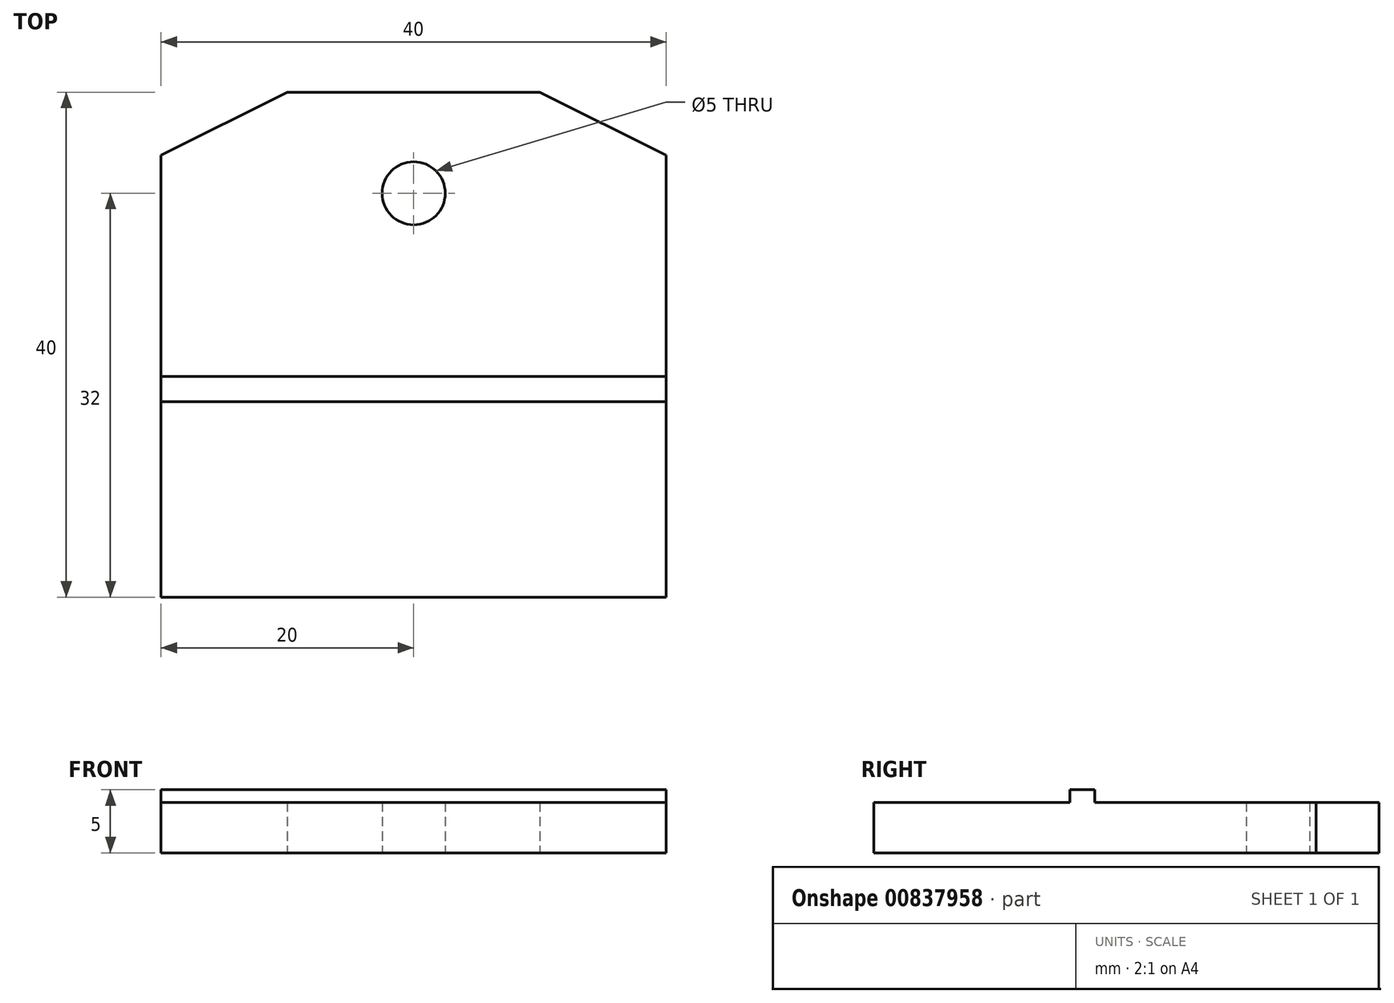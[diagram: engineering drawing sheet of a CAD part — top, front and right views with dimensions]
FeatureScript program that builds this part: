
annotation { "Feature Type Name" : "Feature", "Feature Type Description" : "" }
export const myFeature = defineFeature(function(context is Context, id is Id, definition is map)
    precondition{}
    {
        {
            var Q0;
            Q0=qCreatedBy(makeId("Top.planeOp"),FACE);
            var sketch = newSketch(context, id + "F0", { "sketchPlane" : qUnion([Q0])});
            skLineSegment(sketch, "E0.bottom", {"start": v(0, 0) * mm, "end": v(40, 0) * mm});
            skLineSegment(sketch, "E0.top", {"start": v(10, 40) * mm, "end": v(30, 40) * mm});
            skLineSegment(sketch, "E0.left", {"start": v(0, 0) * mm, "end": v(0, 35) * mm});
            skLineSegment(sketch, "E0.right", {"start": v(40, 0) * mm, "end": v(40, 35) * mm});
            skLineSegment(sketch, "E1", {"start": v(20, 40) * mm, "end": v(20, 0) * mm, "construction": true});
            skLineSegment(sketch, "E2", {"start": v(10, 0) * mm, "end": v(10, 40) * mm, "construction": true});
            skLineSegment(sketch, "E3", {"start": v(0, 35) * mm, "end": v(10, 40) * mm});
            skLineSegment(sketch, "E4.MirrorCS", {"start": v(40, 35) * mm, "end": v(30, 40) * mm});
            skPoint(sketch, "E5.orphan", {"position": v(40, 40) * mm});
            skPoint(sketch, "E6.orphan", {"position": v(0, 40) * mm});
            skCircle(sketch, "E7", {"center": v(20, 32) * mm, "radius": 2.5 * mm});
            skSolve(sketch);
        }
        {
            var Q0;
            Q0=makeQuery(id+"F0.imprint","IMPRINT",FACE,{"disambiguationData":[TD([[makeQuery(id+"F0.imprint","IMPRINT",EDGE,{"derivedFrom":sQuery(id+"F0.wireOp",EDGE,"E0.bottom")}),1.0]])]});
            extrude(context, id + "F1", {"entities" : qUnion([Q0]), "depth" : 4 * mm, "offsetDistance" : 25 * mm});
        }
        {
            var Q0;
            Q0=makeQuery(id+"F1.opExtrude","CAP_FACE",FACE,{"disambiguationData":[OSD([sQuery(id+"F0.wireOp",EDGE,"E0.bottom"),sQuery(id+"F0.wireOp",EDGE,"E0.top"),sQuery(id+"F0.wireOp",EDGE,"E0.left"),sQuery(id+"F0.wireOp",EDGE,"E0.right"),sQuery(id+"F0.wireOp",EDGE,"E3"),sQuery(id+"F0.wireOp",EDGE,"E4.MirrorCS"),sQuery(id+"F0.wireOp",EDGE,"E7")])],"isStart":false});
            var sketch = newSketch(context, id + "F2", { "sketchPlane" : qUnion([Q0])});
            skLineSegment(sketch, "E8", {"start": v(0, 17.5) * mm, "end": v(40, 17.5) * mm, "construction": true});
            skLineSegment(sketch, "E9.bottom", {"start": v(0, 17.5) * mm, "end": v(40, 17.5) * mm});
            skLineSegment(sketch, "E9.top", {"start": v(0, 15.5) * mm, "end": v(40, 15.5) * mm});
            skLineSegment(sketch, "E9.left", {"start": v(0, 17.5) * mm, "end": v(0, 15.5) * mm});
            skLineSegment(sketch, "E9.right", {"start": v(40, 17.5) * mm, "end": v(40, 15.5) * mm});
            skSolve(sketch);
        }
        {
            var Q0;
            Q0=makeQuery(id+"F2.imprint","IMPRINT",FACE,{"disambiguationData":[TD([[makeQuery(id+"F2.imprint","IMPRINT",EDGE,{"derivedFrom":sQuery(id+"F2.wireOp",EDGE,"E9.bottom")}),-1.0]])]});
            extrude(context, id + "F3", {"entities" : qUnion([Q0]), "operationType" : NewBodyOperationType.ADD, "depth" : 1 * mm, "offsetDistance" : 25 * mm});
        }
    });
